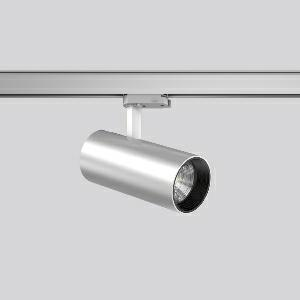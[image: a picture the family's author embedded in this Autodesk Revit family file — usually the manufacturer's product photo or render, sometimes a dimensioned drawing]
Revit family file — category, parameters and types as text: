
# Revit family: deecos_s_mini_742199_004_1_c89d
name_source: partatom
category: Lighting Fixtures
units: mm (PartAtom-declared; Revit-internal decimal feet)

## family parameters
Cut with Voids When Loaded = No
Host = Face
Light Source = No
Part Type = Normal
Room Calculation Point = No
Round Connector Dimension = Use Diameter
Shared = No

## types (1)
- DEECOS S mini (1 x LED Modul 940, 2250 lm, 4000)
    Apparent Load = 20 VA
    Approval mark = CE
    CIE Flux Codes = 96 100 100 100 100
    Color Rendering = 92
    Color Temperature = 4000
    Default Elevation = 1800 mm
    Description = Series: DEECOS S mini
LED surface-mounted projector in modern design with no visible cooling ribs. Housing: die-cast aluminium, powder-coated. Rotation range: 356°. Swivel range: 90°. Black plastic ring and recessed LED to prevent glare from the side. Optical assembly with lens made of plastic (polycarbonate) for the best homogeneous light distribution - can be changed without tools. Best colour rendering index Ra>90. With multi adaptor for 3-circuit tracks 230 V. Suitable for Track on ceiling, Wall track. High quality converter without flickering and stroboscopic effect. The following accessories can be mounted without use of tools: interchangeable lenses, decorative glasses, honeycomb louvre, clear and frosted diffusers, white interchangeable plastic ring. 
Colour: silver
Diameter: 87 mm
Height: 214 mm
Lamp: LED
Socket: without socket
Colour temperature: 4000K
Colour rendering index (CRI): 92
System power: 20 W
Rated luminous flux: 2250 lm
Luminous efficiency: 113 lm/W
Control gear: Regulated power supply
Protection class: I
Type of protection: IP 20
    Height = 214 mm
    Lamp = 1 x LED Modul 940
    Lamp Light Flux = 2250 lm
    Lamp count = 1
    Length = 87 mm
    Lifetime = 50000 h
    Luminous efficacy = 113 lm/W
    Manufacturer = RZB
    ModVariant = No
    Model = 742199.004.1
    Mounting Place = Ceiling
    Mounting Type = Rail mounted
    Number of Poles = 1
    OnlyDefault = Yes
    Power Factor = 1
    Product Name = DEECOS S mini
    Product group = Track mounted projectors
    ProductGroupID = 301
    Protection Class = Protection class I
    Protection Degree = IP 20
    RLX_Detail_Level = 1
    RLX_Emergency_Light_Flux = 0 lm
    RLX_Emergency_Type = 0
    RLX_Emergency_Type_DB = No
    RlxData = <blob elided: 36989 chars, md5=416652ab>
    Socket = socket
    Standby Power = 0 W
    System Light Flux = 2250 lm
    System Power = 20 W
    Type Comments = Product without accessories
    Type Image = 741930.004.jpg
    URL = http://relux.com
    VarID = ---
    Voltage = 230 V
    Voltage Range = 220-240 V
    Weight = 0.00 kg
    Width = 0 mm  [stored 0 ft]

note: [stored X ft] marks values corroborated as IEEE doubles in the binary element streams (Revit-internal decimal feet)

## geometry (parser evidence)
native form markers: Blend x4, Sweep x11
no freeform markers — native parametric forms only
